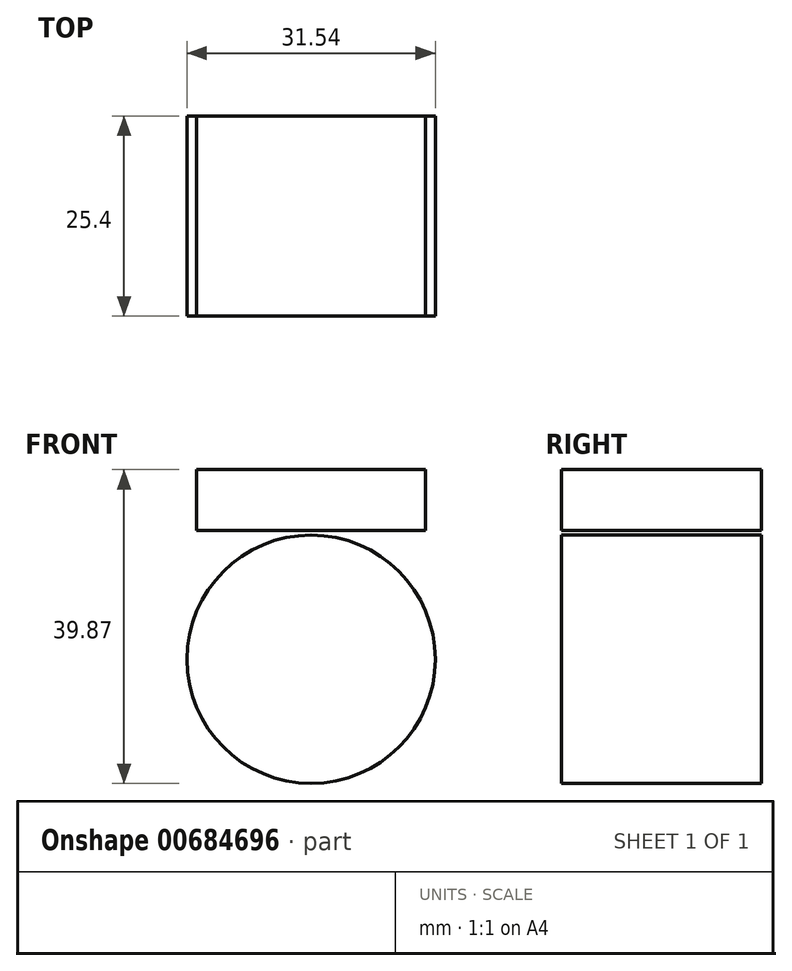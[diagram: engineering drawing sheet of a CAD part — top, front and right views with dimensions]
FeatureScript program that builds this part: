
annotation { "Feature Type Name" : "Feature", "Feature Type Description" : "" }
export const myFeature = defineFeature(function(context is Context, id is Id, definition is map)
    precondition{}
    {
        {
            var Q0;
            Q0=qCreatedBy(makeId("Front.planeOp"),FACE);
            var sketch = newSketch(context, id + "F0", { "sketchPlane" : qUnion([Q0])});
            skCircle(sketch, "E0", {"center": v(-33.43, 17.74) * mm, "radius": 15.77 * mm});
            skLineSegment(sketch, "E1.bottom", {"start": v(-47.98, 41.84) * mm, "end": v(-18.88, 41.84) * mm});
            skLineSegment(sketch, "E1.top", {"start": v(-47.98, 34.11) * mm, "end": v(-18.88, 34.11) * mm});
            skLineSegment(sketch, "E1.left", {"start": v(-47.98, 41.84) * mm, "end": v(-47.98, 34.11) * mm});
            skLineSegment(sketch, "E1.right", {"start": v(-18.88, 41.84) * mm, "end": v(-18.88, 34.11) * mm});
            skSolve(sketch);
        }
        {
            var Q0;
            Q0=qSketchRegion(id+"F0",true);
            extrude(context, id + "F1", {"entities" : qUnion([Q0]), "depth" : 25.4 * mm, "offsetDistance" : 25.4 * mm});
        }
    });
